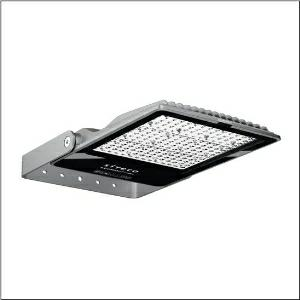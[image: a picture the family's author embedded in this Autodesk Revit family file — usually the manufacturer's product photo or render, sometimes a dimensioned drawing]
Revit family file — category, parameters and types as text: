
# Revit family: sicompact_r__31_midi___pl32_5xa7581e1k23_f752
name_source: partatom
category: Lighting Fixtures
units: mm (PartAtom-declared; Revit-internal decimal feet)

## family parameters
Cut with Voids When Loaded = No
Host = Face
Light Source = No
Part Type = Normal
Room Calculation Point = No
Round Connector Dimension = Use Diameter
Shared = No

## types (1)
- SiCompact® 31 midi  PL32 (1 x LED, 37000 lm, 250 W, 3000K)
    Apparent Load = 250 VA
    CIE Flux Codes = 32 69 98 100 100
    Color Rendering = 70
    Color Temperature = 3000K
    Default Elevation = 1800 mm
    Description = SiCompact® 31 midi, floodlight, primary light control with lens, of plastic, of toughened safety glass, transparent, light distribution: PL32, light emission: direct distribution, primary light characteristic: asymmetric, installation type: surface-mounted, LED, High Power LED, rated luminous flux: 37.000lm, luminous efficacy: 148lm/W, light colour: 730, colour temperature: 3000K, control gear: ON/OFF, with cable, 3x 1.5mm², mains connection: 220..240V, AC, 50/60Hz, connection cable pre-assembled, cable length: 2m, rated input power: 250W, of diecast aluminium, specular, metallic grey (RAL 9006), length: 560mm, width: 330mm, height: 62mm, bracket, of sheet steel, coated, metallic grey (RAL 9006), ON/OFF, protection rating (complete): IP66, insulation class (complete): insulation class I (protective earthing), certification: CE, ENEC, impact resistance: IK08, permissible operating ambient temperature: -40..+45°C, packaging unit: 1 piece

Light Distribution: PL32
    Height = 62 mm  [stored 0.203412 ft]
    Lamp = 1 x LED
    Lamp Light Flux = 37000 lm
    Lamp Power = 250 W
    Lamp count = 1
    Length = 560 mm
    Luminous efficacy = 148 lm/W
    Manufacturer = Siteco
    ModVariant = No
    Model = 5XA7581E1K23
    Mounting Place = Wall
    Mounting Type = Surface mounted
    Number of Poles = 1
    OnlyDefault = Yes
    Power Factor = 1
    Product Name = SiCompact® 31 midi | PL32
    Product group = floodlight | wall mounted
    ProductGroupID = 2001
    Protection Class = Protection class I
    Protection Degree = IP 66
    RLX_Detail_Level = 1
    RLX_Emergency_Light_Flux = 0 lm
    RLX_Emergency_Type = 0
    RLX_Emergency_Type_DB = No
    RlxData = <blob elided: 97789 chars, md5=77344087>
    Socket = socket
    Standby Power = 0 W
    System Light Flux = 37000 lm
    System Power = 250 W
    Type Comments = Product without accessories
    Type Image = l_1006415.jpg
    URL = http://relux.com
    VarID = ---
    Voltage = 0 V
    Weight = 0.00 kg
    Width = 333 mm

note: [stored X ft] marks values corroborated as IEEE doubles in the binary element streams (Revit-internal decimal feet)

## geometry (parser evidence)
native form markers: Blend x4, Sweep x11
no freeform markers — native parametric forms only
